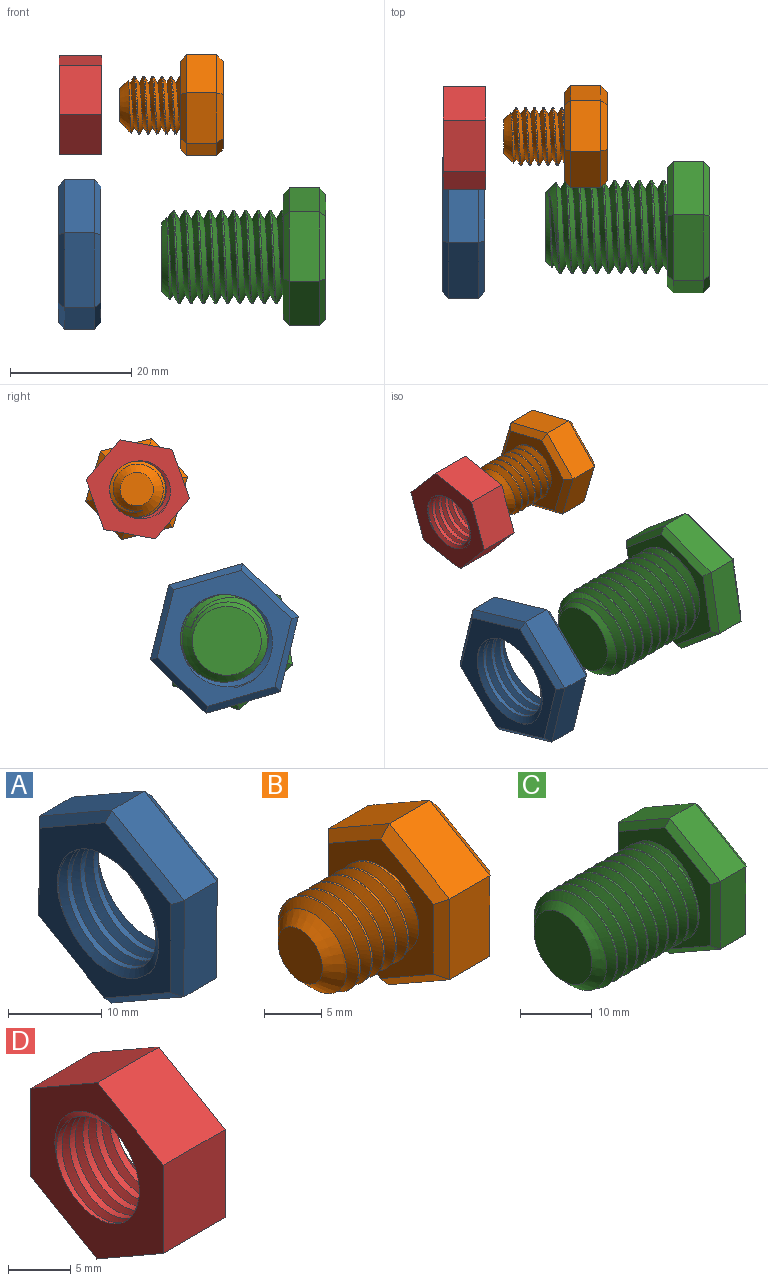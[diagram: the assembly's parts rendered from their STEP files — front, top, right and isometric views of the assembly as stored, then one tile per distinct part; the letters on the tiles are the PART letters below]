
ASSEMBLY  parts=4 mates=2
PART A: 23 faces, bbox 9.3x22.7x26 mm
  f0: cylinder r=7.24mm len=14.48mm, axis (1,0,0), area 111.6mm2, adj f7,f8,f21,f22
  f1: plane 10.98x6.38mm, normal (0,-0.5,0.86), area 63.5mm2, adj f2,f6,f14,f18
  f2: plane 12.7x5mm, normal (0,-1,0), area 63.5mm2, adj f1,f3,f12,f16
  f3: plane 11.02x6.32mm, normal (0,-0.5,-0.87), area 63.5mm2, adj f2,f4,f10,f15
  f4: plane 10.98x6.38mm, normal (0,0.5,-0.86), area 63.5mm2, adj f3,f5,f9,f17
  f5: plane 12.7x5mm, normal (0,1,0), area 63.5mm2, adj f4,f6,f11,f19
  f6: plane 11.02x6.32mm, normal (0,0.5,0.87), area 63.5mm2, adj f1,f5,f13,f20
  f7: plane 23.73x20.67mm, normal (-1,0,0), area 164.4mm2, adj f0,f9,f10,f11,f12,f13,f14,f21
  f8: plane 23.73x20.67mm, normal (1,0,0), area 164.4mm2, adj f0,f15,f16,f17,f18,f19,f20,f21
  f9: plane 10.99x6.96mm, normal (-0.71,0.36,-0.61), area 17.1mm2, adj f4,f7,f10,f11
  f10: plane 11.02x6.9mm, normal (-0.71,-0.35,-0.61), area 17.1mm2, adj f3,f7,f9,f12
  f11: plane 12.7x1.03mm, normal (-0.71,0.71,0), area 17.1mm2, adj f5,f7,f9,f13
  f12: plane 12.7x1.03mm, normal (-0.71,-0.71,0), area 17.1mm2, adj f2,f7,f10,f14
  f13: plane 11.02x6.9mm, normal (-0.71,0.35,0.61), area 17.1mm2, adj f6,f7,f11,f14
  f14: plane 10.99x6.96mm, normal (-0.71,-0.36,0.61), area 17.1mm2, adj f1,f7,f12,f13
  f15: plane 11.02x6.9mm, normal (0.71,-0.35,-0.61), area 17.1mm2, adj f3,f8,f16,f17
  f16: plane 12.7x1.03mm, normal (0.71,-0.71,0), area 17.1mm2, adj f2,f8,f15,f18
  f17: plane 10.99x6.96mm, normal (0.71,0.36,-0.61), area 17.1mm2, adj f4,f8,f15,f19
  f18: plane 10.99x6.96mm, normal (0.71,-0.36,0.61), area 17.1mm2, adj f1,f8,f16,f20
  f19: plane 12.7x1.03mm, normal (0.71,0.71,0), area 17.1mm2, adj f5,f8,f17,f20
  f20: plane 11.02x6.9mm, normal (0.71,0.35,0.61), area 17.1mm2, adj f6,f8,f18,f19
  f21: bspline ~19.31x16.73mm, area 223mm2, adj f0,f7,f8,f22
  f22: bspline ~19.31x16.73mm, area 223mm2, adj f0,f7,f8,f21
PART B: 25 faces, bbox 17.8x15.9x18.1 mm
  f0: cylinder r=4.75mm len=9.5mm, axis (1,0,0), area 28.1mm2, adj f1,f2,f4,f12
  f1: bspline ~10.97x9.91mm, area 196.7mm2, adj f0,f2,f4,f12
  f2: bspline ~10.97x10.66mm, area 196.6mm2, adj f0,f1,f4,f12
  f3: plane 5.5x5.5mm, normal (-1,0,0), area 23.8mm2, adj f4
  f4: cone r=4.75mm half-angle=45deg, axis (1,0,0), area 47.4mm2, adj f0,f1,f2,f3
  f5: plane 7.48x5mm, normal (0,-0.5,0.86), area 43.3mm2, adj f6,f10,f18,f22
  f6: plane 8.66x5mm, normal (0,-1,0), area 43.3mm2, adj f5,f7,f16,f20
  f7: plane 7.52x5mm, normal (0,-0.5,-0.87), area 43.3mm2, adj f6,f8,f14,f19
  f8: plane 7.48x5mm, normal (0,0.5,-0.86), area 43.3mm2, adj f7,f9,f13,f21
  f9: plane 8.66x5mm, normal (0,1,0), area 43.3mm2, adj f8,f10,f15,f23
  f10: plane 7.52x5mm, normal (0,0.5,0.87), area 43.3mm2, adj f5,f9,f17,f24
  f11: plane 15.01x13.03mm, normal (1,0,0), area 146.4mm2, adj f13,f14,f15,f16,f17,f18
  f12: plane 15.83x13.85mm, normal (-1,0,0), area 89.2mm2, adj f0,f1,f2,f19,f20,f21,f22,f23
  f13: plane 7.49x4.93mm, normal (0.71,0.36,-0.61), area 11.4mm2, adj f8,f11,f14,f15
  f14: plane 7.52x4.88mm, normal (0.71,-0.35,-0.61), area 11.4mm2, adj f7,f11,f13,f16
  f15: plane 8.66x1.03mm, normal (0.71,0.71,0), area 11.4mm2, adj f9,f11,f13,f17
  f16: plane 8.66x1.03mm, normal (0.71,-0.71,0), area 11.4mm2, adj f6,f11,f14,f18
  f17: plane 7.52x4.88mm, normal (0.71,0.35,0.61), area 11.4mm2, adj f10,f11,f15,f18
  f18: plane 7.49x4.93mm, normal (0.71,-0.36,0.61), area 11.4mm2, adj f5,f11,f16,f17
  f19: plane 7.52x4.88mm, normal (-0.71,-0.35,-0.61), area 11.4mm2, adj f7,f12,f20,f21
  f20: plane 8.66x1.03mm, normal (-0.71,-0.71,0), area 11.4mm2, adj f6,f12,f19,f22
  f21: plane 7.49x4.93mm, normal (-0.71,0.36,-0.61), area 11.4mm2, adj f8,f12,f19,f23
  f22: plane 7.49x4.93mm, normal (-0.71,-0.36,0.61), area 11.4mm2, adj f5,f12,f20,f24
  f23: plane 8.66x1.03mm, normal (-0.71,0.71,0), area 11.4mm2, adj f9,f12,f21,f24
  f24: plane 7.52x4.88mm, normal (-0.71,0.35,0.61), area 11.4mm2, adj f10,f12,f22,f23
PART C: 26 faces, bbox 27.7x20x23.1 mm
  f0: cylinder r=7.68mm len=18mm, axis (1,0,0), area 139.1mm2, adj f1,f2,f5,f13
  f1: bspline ~20.88x17.74mm, area 713.8mm2, adj f0,f2,f4,f5,f13
  f2: bspline ~21.88x17.74mm, area 715.1mm2, adj f0,f1,f4,f5,f13
  f3: plane 11.36x11.36mm, normal (-1,0,0), area 101.4mm2, adj f4
  f4: cone r=7.68mm half-angle=45deg, axis (1,0,0), area 63.2mm2, adj f1,f2,f3,f5
  f5: cone r=7.68mm half-angle=45deg, axis (1,0,0), area 13.2mm2, adj f0,f1,f2,f4
  f6: plane 9.98x5.81mm, normal (0,-0.5,0.86), area 57.7mm2, adj f7,f11,f19,f23
  f7: plane 11.55x5mm, normal (0,-1,0), area 57.7mm2, adj f6,f8,f17,f21
  f8: plane 10.02x5.74mm, normal (0,-0.5,-0.87), area 57.7mm2, adj f7,f9,f15,f20
  f9: plane 9.98x5.81mm, normal (0,0.5,-0.86), area 57.7mm2, adj f8,f10,f14,f22
  f10: plane 11.55x5mm, normal (0,1,0), area 57.7mm2, adj f9,f11,f16,f24
  f11: plane 10.02x5.74mm, normal (0,0.5,0.87), area 57.7mm2, adj f6,f10,f18,f25
  f12: plane 20.78x18.04mm, normal (1,0,0), area 280.6mm2, adj f14,f15,f16,f17,f18,f19
  f13: plane 20.78x18.04mm, normal (-1,0,0), area 125.2mm2, adj f0,f1,f2,f20,f21,f22,f23,f24
  f14: plane 9.98x6.38mm, normal (0.71,0.36,-0.61), area 15.5mm2, adj f9,f12,f15,f16
  f15: plane 10.02x6.32mm, normal (0.71,-0.35,-0.61), area 15.5mm2, adj f8,f12,f14,f17
  f16: plane 11.55x1.04mm, normal (0.71,0.71,0), area 15.5mm2, adj f10,f12,f14,f18
  f17: plane 11.55x1.04mm, normal (0.71,-0.71,0), area 15.5mm2, adj f7,f12,f15,f19
  f18: plane 10.02x6.32mm, normal (0.71,0.35,0.61), area 15.5mm2, adj f11,f12,f16,f19
  f19: plane 9.98x6.38mm, normal (0.71,-0.36,0.61), area 15.5mm2, adj f6,f12,f17,f18
  f20: plane 10.02x6.32mm, normal (-0.71,-0.35,-0.61), area 15.5mm2, adj f8,f13,f21,f22
  f21: plane 11.55x1.04mm, normal (-0.71,-0.71,0), area 15.5mm2, adj f7,f13,f20,f23
  f22: plane 9.98x6.38mm, normal (-0.71,0.36,-0.61), area 15.5mm2, adj f9,f13,f20,f24
  f23: plane 9.98x6.38mm, normal (-0.71,-0.36,0.61), area 15.5mm2, adj f6,f13,f21,f25
  f24: plane 11.55x1.04mm, normal (-0.71,0.71,0), area 15.5mm2, adj f10,f13,f22,f25
  f25: plane 10.02x6.32mm, normal (-0.71,0.35,0.61), area 15.5mm2, adj f11,f13,f23,f24
PART D: 11 faces, bbox 9.1x15.4x17.7 mm
  f0: plane 7.49x7mm, normal (0,-0.5,0.86), area 60.6mm2, adj f1,f5,f6,f7
  f1: plane 8.66x7mm, normal (0,-1,0), area 60.6mm2, adj f0,f2,f6,f7
  f2: plane 7.51x7mm, normal (0,-0.5,-0.87), area 60.6mm2, adj f1,f3,f6,f7
  f3: plane 7.49x7mm, normal (0,0.5,-0.86), area 60.6mm2, adj f2,f4,f6,f7
  f4: plane 8.66x7mm, normal (0,1,0), area 60.6mm2, adj f3,f5,f6,f7
  f5: plane 7.51x7mm, normal (0,0.5,0.87), area 60.6mm2, adj f0,f4,f6,f7
  f6: plane 17.68x15.39mm, normal (-1,0,0), area 119.9mm2, adj f0,f1,f2,f3,f4,f5,f8,f9
  f7: plane 17.68x15.39mm, normal (1,0,0), area 119.9mm2, adj f0,f1,f2,f3,f4,f5,f8,f9
  f8: cylinder r=4.66mm len=9.32mm, axis (1,0,0), area 85.4mm2, adj f6,f7,f9,f10
  f9: bspline ~12.5x10.82mm, area 128.4mm2, adj f6,f7,f8,f10
  f10: bspline ~12.5x10.82mm, area 128.5mm2, adj f6,f7,f8,f9
PLACE A rot(axis=(0,0.6,-0.8),180deg) t=(-55.27,-6.86,23.48)mm fixed
PLACE B rot(axis=(-1,0,0),43.8deg) t=(-31.66,7.59,48.06)mm
PLACE C rot(axis=(1,0,0),109.9deg) t=(-14.77,-7.25,23.06)mm
PLACE D rot(axis=(1,0,0),100.2deg) t=(-48.16,7.38,48.02)mm fixed
MATE cylindrical C.f0 <-> A.f7  axis (-1,0,0) through (-38.27,-7.25,23.06)mm
MATE cylindrical B.f0 <-> D.f6  axis (-1,0,0) through (-45.16,7.59,48.06)mm
